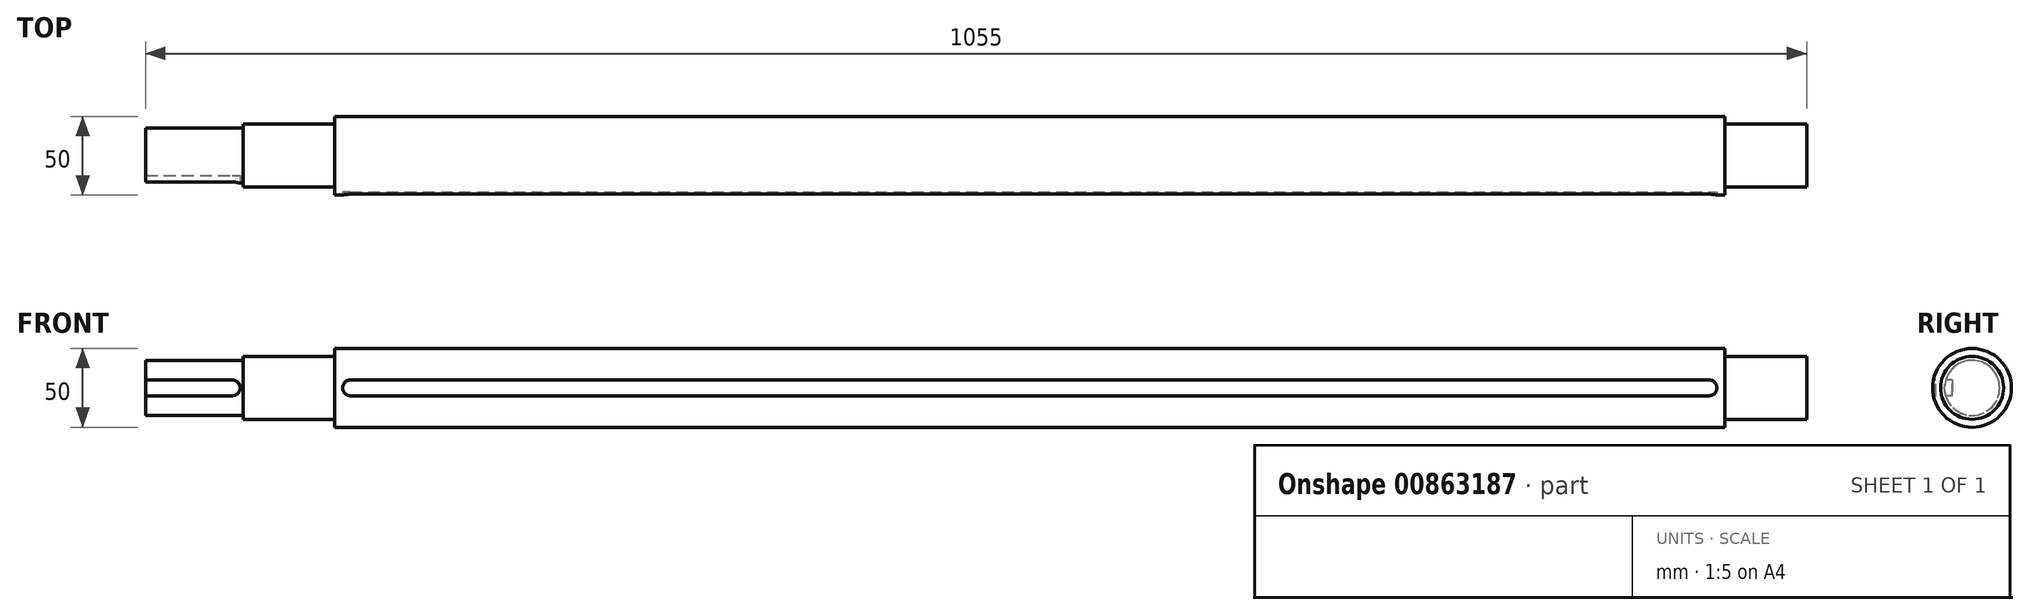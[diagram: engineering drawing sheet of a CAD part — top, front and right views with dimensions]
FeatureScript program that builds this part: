
annotation { "Feature Type Name" : "Feature", "Feature Type Description" : "" }
export const myFeature = defineFeature(function(context is Context, id is Id, definition is map)
    precondition{}
    {
        {
            var Q0;
            Q0=qCreatedBy(makeId("Front.planeOp"),FACE);
            cPlane(context, id + "F0", {"entities" : qUnion([Q0]), "cplaneType" : CPlaneType.OFFSET, "offset" : (35 / 2) * mm, "width" : 150 * mm, "height" : 150 * mm});
        }
        {
            var Q0;
            Q0=qCreatedBy(makeId("Front.planeOp"),FACE);
            cPlane(context, id + "F1", {"entities" : qUnion([Q0]), "cplaneType" : CPlaneType.OFFSET, "offset" : 25 * mm, "width" : 150 * mm, "height" : 150 * mm});
        }
        {
            var Q0;
            Q0=qCreatedBy(makeId("Front.planeOp"),FACE);
            var sketch = newSketch(context, id + "F2", { "sketchPlane" : qUnion([Q0])});
            skLineSegment(sketch, "E0", {"start": v(0, 0) * mm, "end": v(1055, 0) * mm});
            skLineSegment(sketch, "E1", {"start": v(1055, 0) * mm, "end": v(1055, -20) * mm});
            skLineSegment(sketch, "E2", {"start": v(1055, -20) * mm, "end": v(1003, -20) * mm});
            skLineSegment(sketch, "E3", {"start": v(1003, -20) * mm, "end": v(1003, -25) * mm});
            skLineSegment(sketch, "E4", {"start": v(1003, -25) * mm, "end": v(120, -25) * mm});
            skLineSegment(sketch, "E5", {"start": v(120, -25) * mm, "end": v(120, -20) * mm});
            skLineSegment(sketch, "E6", {"start": v(120, -20) * mm, "end": v(62, -20) * mm});
            skLineSegment(sketch, "E7", {"start": v(0, -17.5) * mm, "end": v(0, 0) * mm});
            skLineSegment(sketch, "E8", {"start": v(0, -17.5) * mm, "end": v(62, -17.5) * mm});
            skLineSegment(sketch, "E9", {"start": v(62, -17.5) * mm, "end": v(62, -20) * mm});
            skSolve(sketch);
        }
        {
            var Q0;
            Q0=makeQuery(id+"F2.imprint","IMPRINT",FACE,{"disambiguationData":[TD([[makeQuery(id+"F2.imprint","IMPRINT",EDGE,{"derivedFrom":sQuery(id+"F2.wireOp",EDGE,"E0")}),-1.0]])]});
            var Q1;
            Q1=sQuery(id+"F2.wireOp",EDGE,"E0");
            revolve(context, id + "F3", {"surfaceOperationType" : NewSurfaceOperationType.NEW, "entities" : qUnion([Q0]), "axis" : qUnion([Q1]), "revolveType" : RevolveType.FULL});
        }
        {
            var Q0;
            Q0=qCreatedBy(id+"F0.planeOp",FACE);
            var sketch = newSketch(context, id + "F4", { "sketchPlane" : qUnion([Q0])});
            skLineSegment(sketch, "E10.bottom", {"start": v(0, 5) * mm, "end": v(55, 5) * mm});
            skLineSegment(sketch, "E10.top", {"start": v(0, -5) * mm, "end": v(55, -5) * mm});
            skLineSegment(sketch, "E10.left", {"start": v(0, 5) * mm, "end": v(0, -5) * mm});
            skArc(sketch, "E11", {"start": v(55, -5) * mm, "mid": v(60, 0) * mm, "end": v(55, 5) * mm});
            skSolve(sketch);
        }
        {
            var Q0;
            Q0 = qSketchRegion(id + "F4", true);
            extrude(context, id + "F5", {"entities" : qUnion([Q0]), "operationType" : NewBodyOperationType.REMOVE, "oppositeDirection" : true, "depth" : 5 * mm, "offsetDistance" : 25 * mm});
        }
        {
            var Q0;
            Q0=qCreatedBy(id+"F1.planeOp",FACE);
            var sketch = newSketch(context, id + "F6", { "sketchPlane" : qUnion([Q0])});
            skLineSegment(sketch, "E12.bottom", {"start": v(130, 5) * mm, "end": v(993, 5) * mm});
            skLineSegment(sketch, "E12.top", {"start": v(130, -5) * mm, "end": v(993, -5) * mm});
            skArc(sketch, "E13", {"start": v(993, -5) * mm, "mid": v(998, 0) * mm, "end": v(993, 5) * mm});
            skArc(sketch, "E14", {"start": v(130, 5) * mm, "mid": v(125, 0) * mm, "end": v(130, -5) * mm});
            skSolve(sketch);
        }
        {
            var Q0;
            Q0 = qSketchRegion(id + "F6", true);
            extrude(context, id + "F7", {"entities" : qUnion([Q0]), "operationType" : NewBodyOperationType.REMOVE, "oppositeDirection" : true, "depth" : 2 * mm, "offsetDistance" : 25 * mm});
        }
    });
